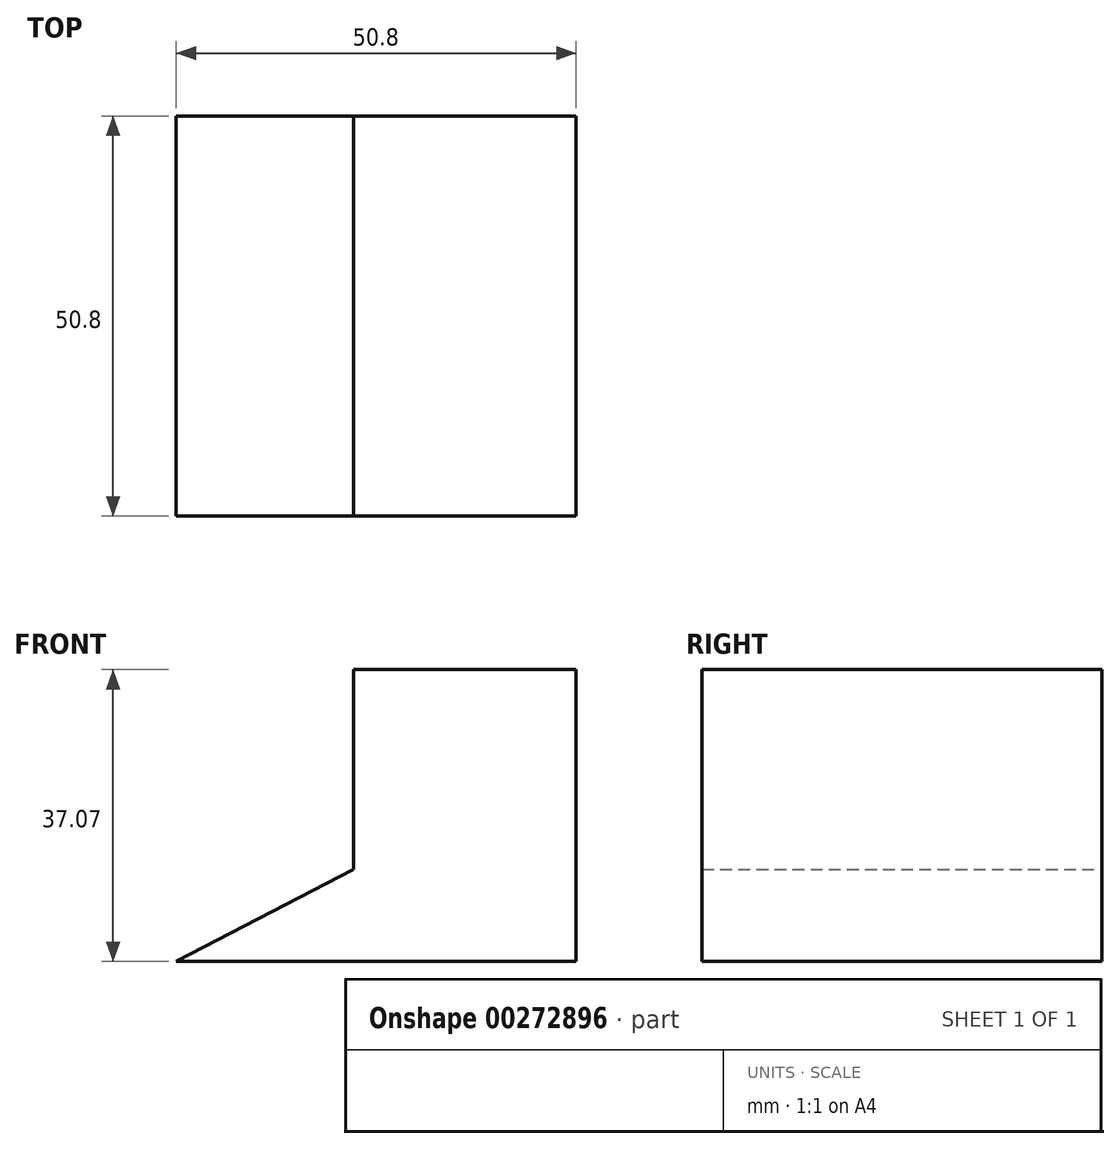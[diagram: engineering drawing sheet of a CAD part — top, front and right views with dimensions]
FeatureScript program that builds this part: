
annotation { "Feature Type Name" : "Feature", "Feature Type Description" : "" }
export const myFeature = defineFeature(function(context is Context, id is Id, definition is map)
    precondition{}
    {
        {
            var Q0;
            Q0=qCreatedBy(makeId("Front.planeOp"),FACE);
            var sketch = newSketch(context, id + "F0", { "sketchPlane" : qUnion([Q0])});
            skLineSegment(sketch, "E0", {"start": v(0, 0) * mm, "end": v(-50.8, 0) * mm});
            skLineSegment(sketch, "E1", {"start": v(-50.8, 0) * mm, "end": v(-28.24, 11.67) * mm});
            skLineSegment(sketch, "E2", {"start": v(-28.24, 37.07) * mm, "end": v(-28.24, 11.67) * mm});
            skLineSegment(sketch, "E3", {"start": v(-28.24, 37.07) * mm, "end": v(0, 37.07) * mm});
            skLineSegment(sketch, "E4", {"start": v(0, 37.07) * mm, "end": v(0, 0) * mm});
            skSolve(sketch);
        }
        {
            var Q0;
            Q0=makeQuery(id+"F0.imprint","IMPRINT",FACE,{"disambiguationData":[TD([[makeQuery(id+"F0.imprint","IMPRINT",EDGE,{"derivedFrom":sQuery(id+"F0.wireOp",EDGE,"E0")}),-1.0]])]});
            extrude(context, id + "F1", {"entities" : qUnion([Q0]), "depth" : 50.8 * mm});
        }
    });
